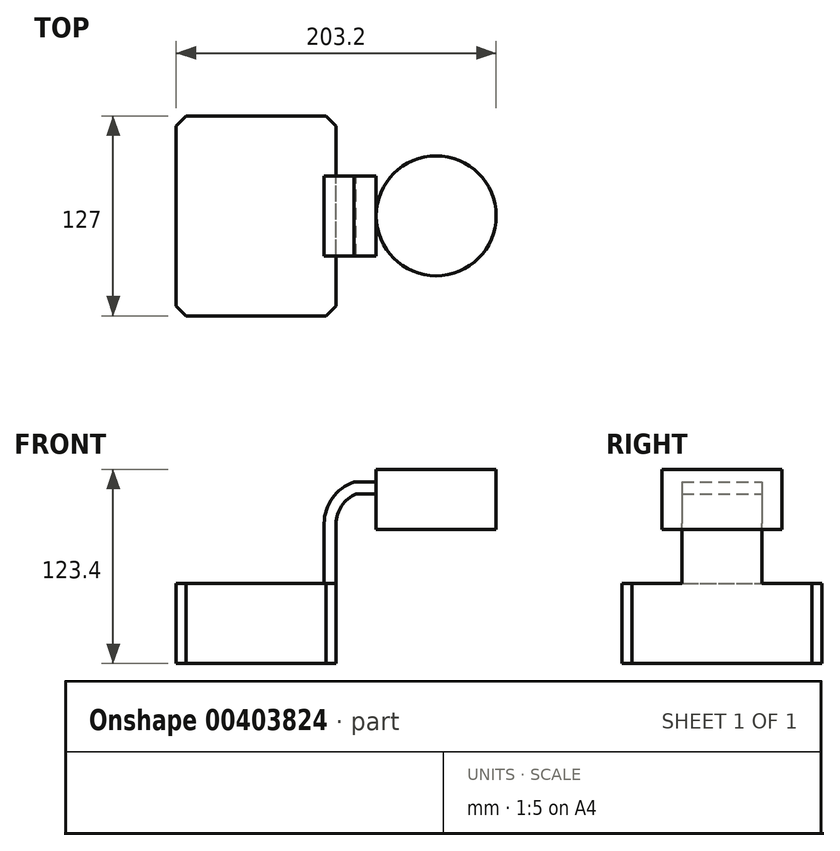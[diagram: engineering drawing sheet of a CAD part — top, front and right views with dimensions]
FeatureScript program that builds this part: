
annotation { "Feature Type Name" : "Feature", "Feature Type Description" : "" }
export const myFeature = defineFeature(function(context is Context, id is Id, definition is map)
    precondition{}
    {
        {
            var Q0;
            Q0=qCreatedBy(makeId("Front.planeOp"),FACE);
            var sketch = newSketch(context, id + "F0", { "sketchPlane" : qUnion([Q0])});
            skLineSegment(sketch, "E0.bottom", {"start": v(-67.2, 11.19) * mm, "end": v(34.4, 11.19) * mm});
            skLineSegment(sketch, "E0.top", {"start": v(-67.2, -39.61) * mm, "end": v(34.4, -39.61) * mm});
            skLineSegment(sketch, "E0.left", {"start": v(-67.2, 11.19) * mm, "end": v(-67.2, -39.61) * mm});
            skLineSegment(sketch, "E0.right", {"start": v(34.4, 11.19) * mm, "end": v(34.4, -39.61) * mm});
            skLineSegment(sketch, "E1.bottom", {"start": v(59.8, 83.8) * mm, "end": v(136, 83.8) * mm});
            skLineSegment(sketch, "E1.top", {"start": v(59.8, 45.7) * mm, "end": v(136, 45.7) * mm});
            skLineSegment(sketch, "E1.left", {"start": v(59.8, 83.8) * mm, "end": v(59.8, 45.7) * mm});
            skLineSegment(sketch, "E1.right", {"start": v(136, 83.8) * mm, "end": v(136, 45.7) * mm});
            skLineSegment(sketch, "E2", {"start": v(34.4, 11.19) * mm, "end": v(34.4, 49.29) * mm});
            skArc(sketch, "E3", {"start": v(34.4, 49.29) * mm, "mid": v(37.86, 60.65) * mm, "end": v(47.1, 68.13) * mm});
            skLineSegment(sketch, "E4", {"start": v(47.1, 68.13) * mm, "end": v(97.9, 68.13) * mm});
            skPoint(sketch, "E4.endSnap0", {"position": v(97.9, 83.8) * mm});
            skLineSegment(sketch, "E5.0", {"start": v(45.73, 75.75) * mm, "end": v(97.9, 75.75) * mm});
            skArc(sketch, "E5.1", {"start": v(26.77, 49.29) * mm, "mid": v(32, 65.56) * mm, "end": v(45.73, 75.75) * mm});
            skLineSegment(sketch, "E5.2", {"start": v(26.77, 11.19) * mm, "end": v(26.77, 49.29) * mm});
            skLineSegment(sketch, "E6", {"start": v(97.9, 75.75) * mm, "end": v(97.9, 45.7) * mm});
            skLineSegment(sketch, "E7", {"start": v(97.9, 75.75) * mm, "end": v(97.9, 83.8) * mm});
            skFitSpline(sketch, "E8", {"points": [v(-67.2, 11.19) * mm, v(45.73, 75.75) * mm], "startDerivative": vector(63.43, 105.02) * mm, "endDerivative": vector(137.2, -8.9) * mm});
            skSolve(sketch);
        }
        {
            var Q0;
            Q0=makeQuery(id+"F0.imprint","IMPRINT",FACE,{"disambiguationData":[TD([[makeQuery(id+"F0.imprint","IMPRINT",EDGE,{"derivedFrom":sQuery(id+"F0.wireOp",EDGE,"E0.top")}),1.0]])]});
            extrude(context, id + "F1", {"entities" : qUnion([Q0]), "endBound" : BoundingType.SYMMETRIC, "depth" : 127 * mm});
        }
        {
            var Q0;
            {var subQ1=sQuery(id+"F0.wireOp",EDGE,"E2");Q0=makeQuery(id+"F0.imprint","IMPRINT",FACE,{"disambiguationData":[TD([[makeQuery(id+"F0.imprint","IMPRINT",EDGE,{"derivedFrom":subQ1}),1.0]])]});}
            extrude(context, id + "F2", {"entities" : qUnion([Q0]), "operationType" : NewBodyOperationType.ADD, "endBound" : BoundingType.SYMMETRIC, "depth" : 50.8 * mm});
        }
        {
            var Q0;
            Q0=makeQuery(id+"F0.imprint","IMPRINT",FACE,{"disambiguationData":[TD([[makeQuery(id+"F0.imprint","IMPRINT",EDGE,{"derivedFrom":sQuery(id+"F0.wireOp",EDGE,"E5.1")}),1.0]])]});
            extrude(context, id + "F3", {"entities" : qUnion([Q0]), "operationType" : NewBodyOperationType.ADD, "endBound" : BoundingType.SYMMETRIC, "depth" : 25.4 * mm});
        }
        {
            var Q0;
            {var subQ0=sQuery(id+"F0.wireOp",EDGE,"E1.right");Q0=makeQuery(id+"F0.imprint","IMPRINT",FACE,{"disambiguationData":[TD([[makeQuery(id+"F0.imprint","IMPRINT",EDGE,{"derivedFrom":subQ0}),-1.0]])]});}
            var Q1;
            Q1=sQuery(id+"F0.wireOp",EDGE,"E7");
            revolve(context, id + "F4", {"operationType" : NewBodyOperationType.ADD, "entities" : qUnion([Q0]), "axis" : qUnion([Q1]), "revolveType" : RevolveType.FULL});
        }
        {
            var Q0;
            Q0=makeQuery(id+"F1.opExtrude","CAP_EDGE",EDGE,{"disambiguationData":[OSD([sQuery(id+"F0.wireOp",EDGE,"E0.right")])],"isStart":false});
            var Q1;
            Q1=makeQuery(id+"F1.opExtrude","CAP_EDGE",EDGE,{"disambiguationData":[OSD([sQuery(id+"F0.wireOp",EDGE,"E0.left")])],"isStart":false});
            var Q2;
            Q2=makeQuery(id+"F1.opExtrude","CAP_EDGE",EDGE,{"disambiguationData":[OSD([sQuery(id+"F0.wireOp",EDGE,"E0.right")])],"isStart":true});
            var Q3;
            Q3=makeQuery(id+"F1.opExtrude","CAP_EDGE",EDGE,{"disambiguationData":[OSD([sQuery(id+"F0.wireOp",EDGE,"E0.left")])],"isStart":true});
            chamfer(context, id + "F5", {"entities" : qUnion([Q0, Q1, Q2, Q3]), "width" : 6.35 * mm, "tangentPropagation" : true});
        }
    });
